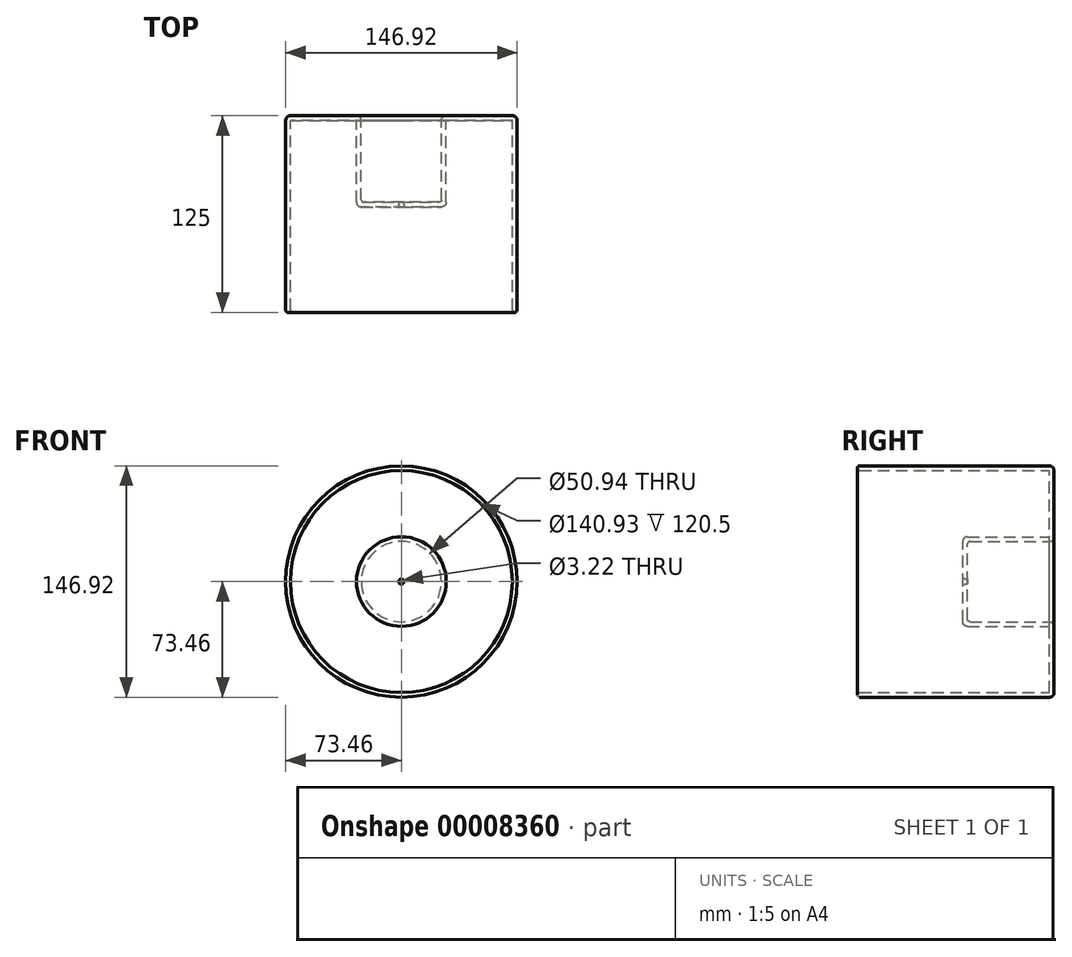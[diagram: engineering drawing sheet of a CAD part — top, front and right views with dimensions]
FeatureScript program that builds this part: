
annotation { "Feature Type Name" : "Feature", "Feature Type Description" : "" }
export const myFeature = defineFeature(function(context is Context, id is Id, definition is map)
    precondition{}
    {
        {
            var Q0;
            Q0=qCreatedBy(makeId("Front.planeOp"),FACE);
            var sketch = newSketch(context, id + "F0", { "sketchPlane" : qUnion([Q0])});
            skCircle(sketch, "E0", {"center": v(0, 0) * mm, "radius": 73.46 * mm});
            skSolve(sketch);
        }
        {
            var Q0;
            Q0 = qSketchRegion(id + "F0", true);
            extrude(context, id + "F1", {"entities" : qUnion([Q0]), "depth" : 100 * mm});
        }
        {
            var Q0;
            Q0=qCreatedBy(makeId("Front.planeOp"),FACE);
            var sketch = newSketch(context, id + "F2", { "sketchPlane" : qUnion([Q0])});
            skCircle(sketch, "E1", {"center": v(0, 0) * mm, "radius": 25.47 * mm});
            skSolve(sketch);
        }
        {
            var Q0;
            Q0=makeQuery(id+"F2.imprint","IMPRINT",FACE,{"disambiguationData":[TD([[makeQuery(id+"F2.imprint","IMPRINT",EDGE,{"derivedFrom":sQuery(id+"F2.wireOp",EDGE,"E1")}),1.0]])]});
            extrude(context, id + "F3", {"entities" : qUnion([Q0]), "operationType" : NewBodyOperationType.REMOVE, "depth" : 30 * mm});
        }
        {
            var Q0;
            Q0=makeQuery(id+"F1.opExtrude","CAP_FACE",FACE,{"disambiguationData":[OSD([sQuery(id+"F0.wireOp",EDGE,"E0")])],"isStart":true});
            extrude(context, id + "F4", {"entities" : qUnion([Q0]), "operationType" : NewBodyOperationType.ADD, "depth" : 25 * mm});
        }
        {
            var Q0;
            Q0=makeQuery(id+"F1.opExtrude","CAP_FACE",FACE,{"disambiguationData":[OSD([sQuery(id+"F0.wireOp",EDGE,"E0")])],"isStart":false});
            shell(context, id + "F5", {"entities" : qUnion([Q0]), "thickness" : 3 * mm});
        }
        {
            var Q0;
            Q0=makeQuery(id+"F3.boolean.opBoolean","COPY",FACE,{"derivedFrom":makeQuery(id+"F3.opExtrude","CAP_FACE",FACE,{"disambiguationData":[OSD([sQuery(id+"F2.wireOp",EDGE,"E1")])],"isStart":false})});
            var sketch = newSketch(context, id + "F6", { "sketchPlane" : qUnion([Q0])});
            skCircle(sketch, "E2", {"center": v(0, 0) * mm, "radius": 1.6 * mm});
            skSolve(sketch);
        }
        {
            var Q0;
            Q0 = qSketchRegion(id + "F6", true);
            extrude(context, id + "F7", {"entities" : qUnion([Q0]), "operationType" : NewBodyOperationType.REMOVE, "endBound" : BoundingType.THROUGH_ALL, "oppositeDirection" : true, "depth" : 25 * mm});
        }
        {
            var Q0;
            {var subQ0=sQuery(id+"F2.wireOp",EDGE,"E1");Q0=makeQuery(id+"F5.opShell","OFFSET_EDGE",EDGE,{"disambiguationData":[OSD([subQ0]),TDD([makeQuery(id+"F3.boolean.opBoolean","COPY",EDGE,{"derivedFrom":makeQuery(id+"F3.opExtrude","CAP_EDGE",EDGE,{"disambiguationData":[OSD([subQ0])],"isStart":false})})])]});}
            fillet(context, id + "F8", {"entities" : qUnion([Q0]), "radius" : 3 * mm, "tangentPropagation" : true, "allowEdgeOverflow" : false});
        }
        {
            var Q0;
            {var subQ0=sQuery(id+"F2.wireOp",EDGE,"E1");Q0=makeQuery(id+"F5.opShell","OFFSET_EDGE",EDGE,{"disambiguationData":[OSD([subQ0]),TDD([makeQuery(id+"F4.opExtrude","CAP_EDGE",EDGE,{"disambiguationData":[OSD([subQ0])],"isStart":false})])]});}
            var Q1;
            {var subQ0=sQuery(id+"F0.wireOp",EDGE,"E0");Q1=makeQuery(id+"F5.opShell","OFFSET_EDGE",EDGE,{"disambiguationData":[OSD([subQ0]),TDD([makeQuery(id+"F1.opExtrude","CAP_EDGE",EDGE,{"disambiguationData":[OSD([subQ0])],"isStart":false})])]});}
            var Q2;
            Q2=makeQuery(id+"F1.opExtrude","CAP_EDGE",EDGE,{"disambiguationData":[OSD([sQuery(id+"F0.wireOp",EDGE,"E0")])],"isStart":false});
            fillet(context, id + "F9", {"entities" : qUnion([Q0, Q1, Q2]), "radius" : 1.5 * mm, "tangentPropagation" : true, "allowEdgeOverflow" : false});
        }
        {
            var Q0;
            Q0=makeQuery(id+"F4.opExtrude","CAP_EDGE",EDGE,{"disambiguationData":[OSD([sQuery(id+"F0.wireOp",EDGE,"E0")])],"isStart":false});
            var Q1;
            Q1=makeQuery(id+"F4.opExtrude","CAP_EDGE",EDGE,{"disambiguationData":[OSD([sQuery(id+"F2.wireOp",EDGE,"E1")])],"isStart":false});
            fillet(context, id + "F10", {"entities" : qUnion([Q0, Q1]), "radius" : 3 * mm, "tangentPropagation" : true, "allowEdgeOverflow" : false});
        }
        {
            var Q0;
            Q0=makeQuery(id+"F3.boolean.opBoolean","COPY",EDGE,{"derivedFrom":makeQuery(id+"F3.opExtrude","CAP_EDGE",EDGE,{"disambiguationData":[OSD([sQuery(id+"F2.wireOp",EDGE,"E1")])],"isStart":false})});
            fillet(context, id + "F11", {"entities" : qUnion([Q0]), "radius" : 1.5 * mm, "tangentPropagation" : true, "allowEdgeOverflow" : false});
        }
        {
            var Q0;
            {var subQ0=sQuery(id+"F2.wireOp",EDGE,"E1");Q0=makeQuery(id+"F7.boolean.opBoolean","INTERSECT",EDGE,{"derivedFrom":[makeQuery(id+"F5.opShell","OFFSET_FACE",FACE,{"disambiguationData":[OSD([subQ0]),TDD([makeQuery(id+"F3.boolean.opBoolean","COPY",FACE,{"derivedFrom":makeQuery(id+"F3.opExtrude","CAP_FACE",FACE,{"disambiguationData":[OSD([subQ0])],"isStart":false})})])]}),makeQuery(id+"F7.opExtrude","SWEPT_FACE",FACE,{"disambiguationData":[OSD([sQuery(id+"F6.wireOp",EDGE,"E2")])]})]});}
            var Q1;
            Q1=makeQuery(id+"F7.boolean.opBoolean","COPY",EDGE,{"derivedFrom":makeQuery(id+"F7.opExtrude","CAP_EDGE",EDGE,{"disambiguationData":[OSD([sQuery(id+"F6.wireOp",EDGE,"E2")])],"isStart":true})});
            fillet(context, id + "F12", {"entities" : qUnion([Q0, Q1]), "radius" : 1.5 * mm, "tangentPropagation" : true, "allowEdgeOverflow" : false});
        }
    });
